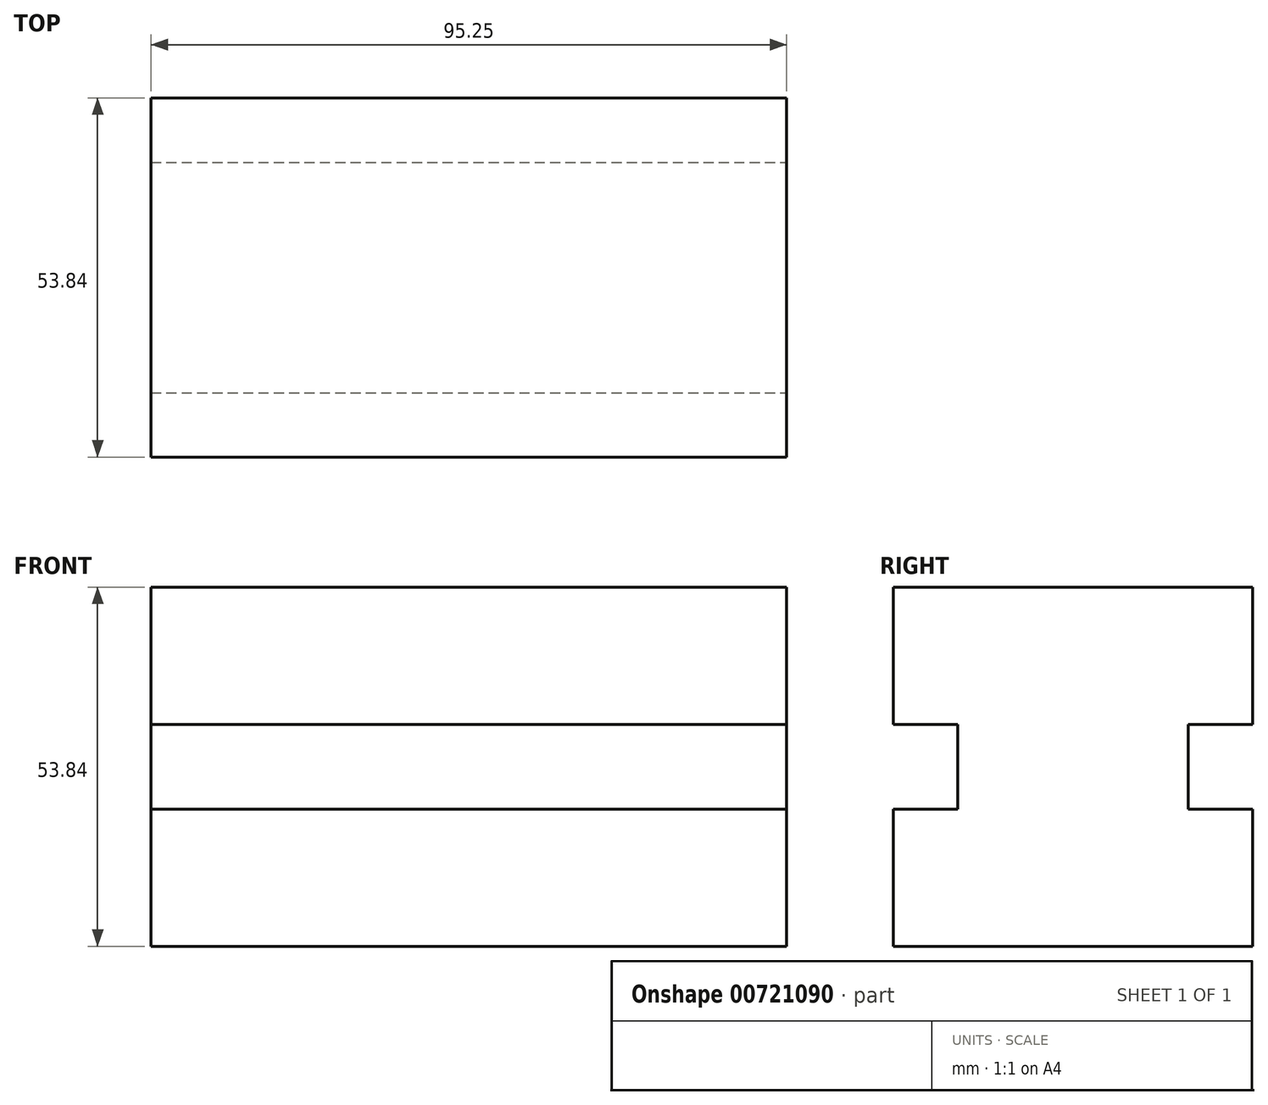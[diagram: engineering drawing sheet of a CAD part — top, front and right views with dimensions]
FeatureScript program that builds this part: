
annotation { "Feature Type Name" : "Feature", "Feature Type Description" : "" }
export const myFeature = defineFeature(function(context is Context, id is Id, definition is map)
    precondition{}
    {
        {
            var Q0;
            Q0=qCreatedBy(makeId("Right.planeOp"),FACE);
            var sketch = newSketch(context, id + "F0", { "sketchPlane" : qUnion([Q0])});
            skLineSegment(sketch, "E0.bottom", {"start": v(26.92, -26.92) * mm, "end": v(-26.92, -26.92) * mm});
            skLineSegment(sketch, "E0.top", {"start": v(26.92, 26.92) * mm, "end": v(-26.92, 26.92) * mm});
            skLineSegment(sketch, "E0.left", {"start": v(26.92, -26.92) * mm, "end": v(26.92, -6.35) * mm});
            skLineSegment(sketch, "E0.right", {"start": v(-26.92, -26.92) * mm, "end": v(-26.92, -6.35) * mm});
            skPoint(sketch, "E0.middle", {"position": v(0, 0) * mm});
            skLineSegment(sketch, "E1.bottom", {"start": v(-26.92, 6.35) * mm, "end": v(-17.27, 6.35) * mm});
            skLineSegment(sketch, "E1.top", {"start": v(-26.92, -6.35) * mm, "end": v(-17.27, -6.35) * mm});
            skLineSegment(sketch, "E1.right", {"start": v(-17.27, 6.35) * mm, "end": v(-17.27, -6.35) * mm});
            skLineSegment(sketch, "E2", {"start": v(0, 32.21) * mm, "end": v(0, -36.4) * mm, "construction": true});
            skLineSegment(sketch, "E3.MirrorCS", {"start": v(26.92, 6.35) * mm, "end": v(17.27, 6.35) * mm});
            skLineSegment(sketch, "E4.MirrorCS", {"start": v(17.27, 6.35) * mm, "end": v(17.27, -6.35) * mm});
            skLineSegment(sketch, "E5.MirrorCS", {"start": v(26.92, -6.35) * mm, "end": v(17.27, -6.35) * mm});
            skLineSegment(sketch, "E6.trimOffspring", {"start": v(26.92, 6.35) * mm, "end": v(26.92, 26.92) * mm});
            skLineSegment(sketch, "E7.trimOffspring", {"start": v(-26.92, 6.35) * mm, "end": v(-26.92, 26.92) * mm});
            skSolve(sketch);
        }
        {
            var Q0;
            Q0=makeQuery(id+"F0.imprint","IMPRINT",FACE,{"disambiguationData":[TD([[makeQuery(id+"F0.imprint","IMPRINT",EDGE,{"derivedFrom":sQuery(id+"F0.wireOp",EDGE,"E0.bottom")}),-1.0]])]});
            extrude(context, id + "F1", {"entities" : qUnion([Q0]), "oppositeDirection" : true, "depth" : 95.25 * mm, "offsetDistance" : 25.4 * mm});
        }
    });
